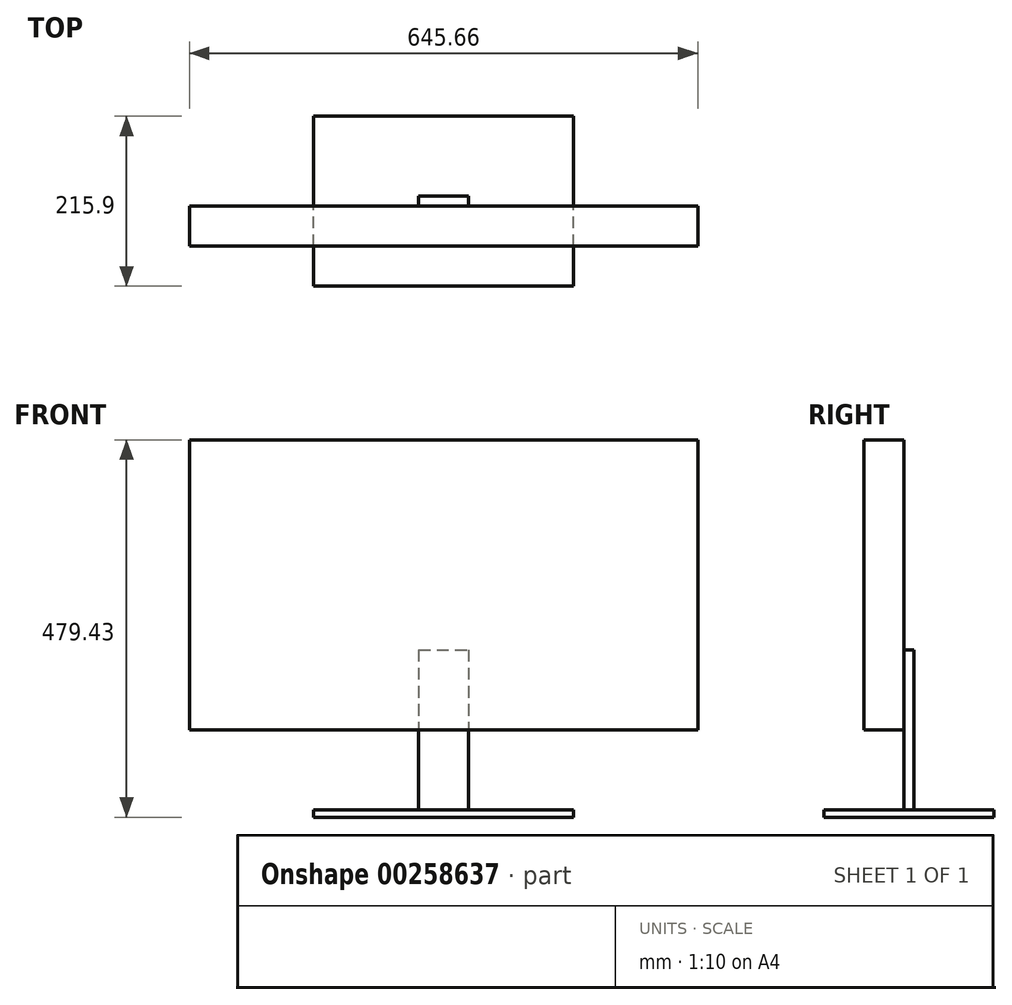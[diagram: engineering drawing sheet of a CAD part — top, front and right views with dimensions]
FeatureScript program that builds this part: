
annotation { "Feature Type Name" : "Feature", "Feature Type Description" : "" }
export const myFeature = defineFeature(function(context is Context, id is Id, definition is map)
    precondition{}
    {
        {
            var Q0;
            Q0=qCreatedBy(makeId("Top.planeOp"),FACE);
            var sketch = newSketch(context, id + "F0", { "sketchPlane" : qUnion([Q0])});
            skLineSegment(sketch, "E0.bottom", {"start": v(0, 0) * mm, "end": v(330.2, 0) * mm});
            skLineSegment(sketch, "E0.top", {"start": v(0, 215.9) * mm, "end": v(330.2, 215.9) * mm});
            skLineSegment(sketch, "E0.left", {"start": v(0, 0) * mm, "end": v(0, 215.9) * mm});
            skLineSegment(sketch, "E0.right", {"start": v(330.2, 0) * mm, "end": v(330.2, 215.9) * mm});
            skSolve(sketch);
        }
        {
            var Q0;
            Q0 = qSketchRegion(id + "F0", true);
            extrude(context, id + "F1", {"entities" : qUnion([Q0]), "depth" : 9.52 * mm});
        }
        {
            var Q0;
            Q0=makeQuery(id+"F1.opExtrude","CAP_FACE",FACE,{"disambiguationData":[OSD([sQuery(id+"F0.wireOp",EDGE,"E0.bottom"),sQuery(id+"F0.wireOp",EDGE,"E0.top"),sQuery(id+"F0.wireOp",EDGE,"E0.left"),sQuery(id+"F0.wireOp",EDGE,"E0.right")])],"isStart":false});
            var sketch = newSketch(context, id + "F2", { "sketchPlane" : qUnion([Q0])});
            skLineSegment(sketch, "E1.bottom", {"start": v(133.35, 114.3) * mm, "end": v(196.85, 114.3) * mm});
            skLineSegment(sketch, "E1.top", {"start": v(133.35, 101.6) * mm, "end": v(196.85, 101.6) * mm});
            skLineSegment(sketch, "E1.left", {"start": v(133.35, 114.3) * mm, "end": v(133.35, 101.6) * mm});
            skLineSegment(sketch, "E1.right", {"start": v(196.85, 114.3) * mm, "end": v(196.85, 101.6) * mm});
            skSolve(sketch);
        }
        {
            var Q0;
            Q0 = qSketchRegion(id + "F2", true);
            extrude(context, id + "F3", {"entities" : qUnion([Q0]), "operationType" : NewBodyOperationType.ADD, "depth" : 203.2 * mm});
        }
        {
            var Q0;
            Q0=makeQuery(id+"F3.opExtrude","SWEPT_FACE",FACE,{"disambiguationData":[OSD([sQuery(id+"F2.wireOp",EDGE,"E1.top")])]});
            var sketch = newSketch(context, id + "F4", { "sketchPlane" : qUnion([Q0])});
            skLineSegment(sketch, "E2.bottom", {"start": v(487.93, 111.13) * mm, "end": v(-157.73, 111.12) * mm});
            skLineSegment(sketch, "E2.top", {"start": v(487.93, 479.43) * mm, "end": v(-157.73, 479.42) * mm});
            skLineSegment(sketch, "E2.left", {"start": v(487.93, 111.13) * mm, "end": v(487.93, 479.43) * mm});
            skLineSegment(sketch, "E2.right", {"start": v(-157.73, 111.12) * mm, "end": v(-157.73, 479.42) * mm});
            skSolve(sketch);
        }
        {
            var Q0;
            Q0 = qSketchRegion(id + "F4", true);
            extrude(context, id + "F5", {"entities" : qUnion([Q0]), "operationType" : NewBodyOperationType.ADD, "depth" : 50.8 * mm});
        }
    });
